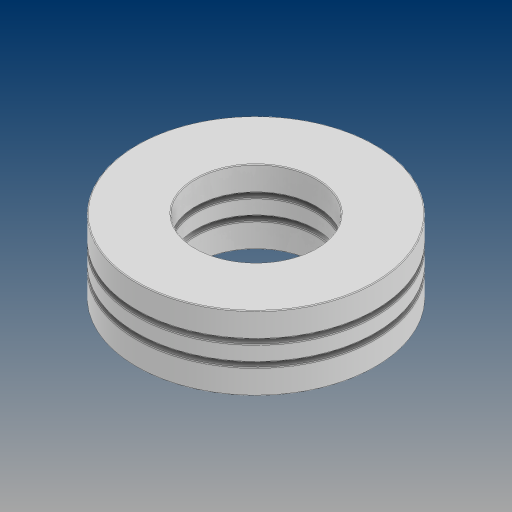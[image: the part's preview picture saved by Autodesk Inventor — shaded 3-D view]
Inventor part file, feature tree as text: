
AUTODESK INVENTOR PART (.ipt)
format: ipt  version: 2024.3 (Build 283343000, 343)  size: 335,872 bytes
history: native  units: in
note: dims shown in document units (in); Inventor stores cm internally (conversion verified against a paired STEP export)
features: fillet x3, other x2, revolve x1
ambient origin geometry x8: Origin, YZ Plane, XZ Plane, XY Plane, X Axis, Y Axis, Z Axis, Center Point
bodies: Solid1 (feature_tree), Solid2 (feature_tree), Solid3 (feature_tree), Solid4 (feature_tree), Solid5 (feature_tree), Solid6 (feature_tree)
feature tree (6):
  revolve  "Revolve2"  [1 undecoded]
  other  "CirPattern1[1]"
  other  "CirPattern1[2]"
  fillet  "Fillet2"  [1 undecoded]
  fillet  "Fillet1"  [1 undecoded]
  fillet  "Fillet3"  [1 undecoded]
note: 4 required parameter values undecoded (feature->parameter linkage not recoverable at this tier; creation-order binding heuristic only, values carry confidence <= 0.55)
